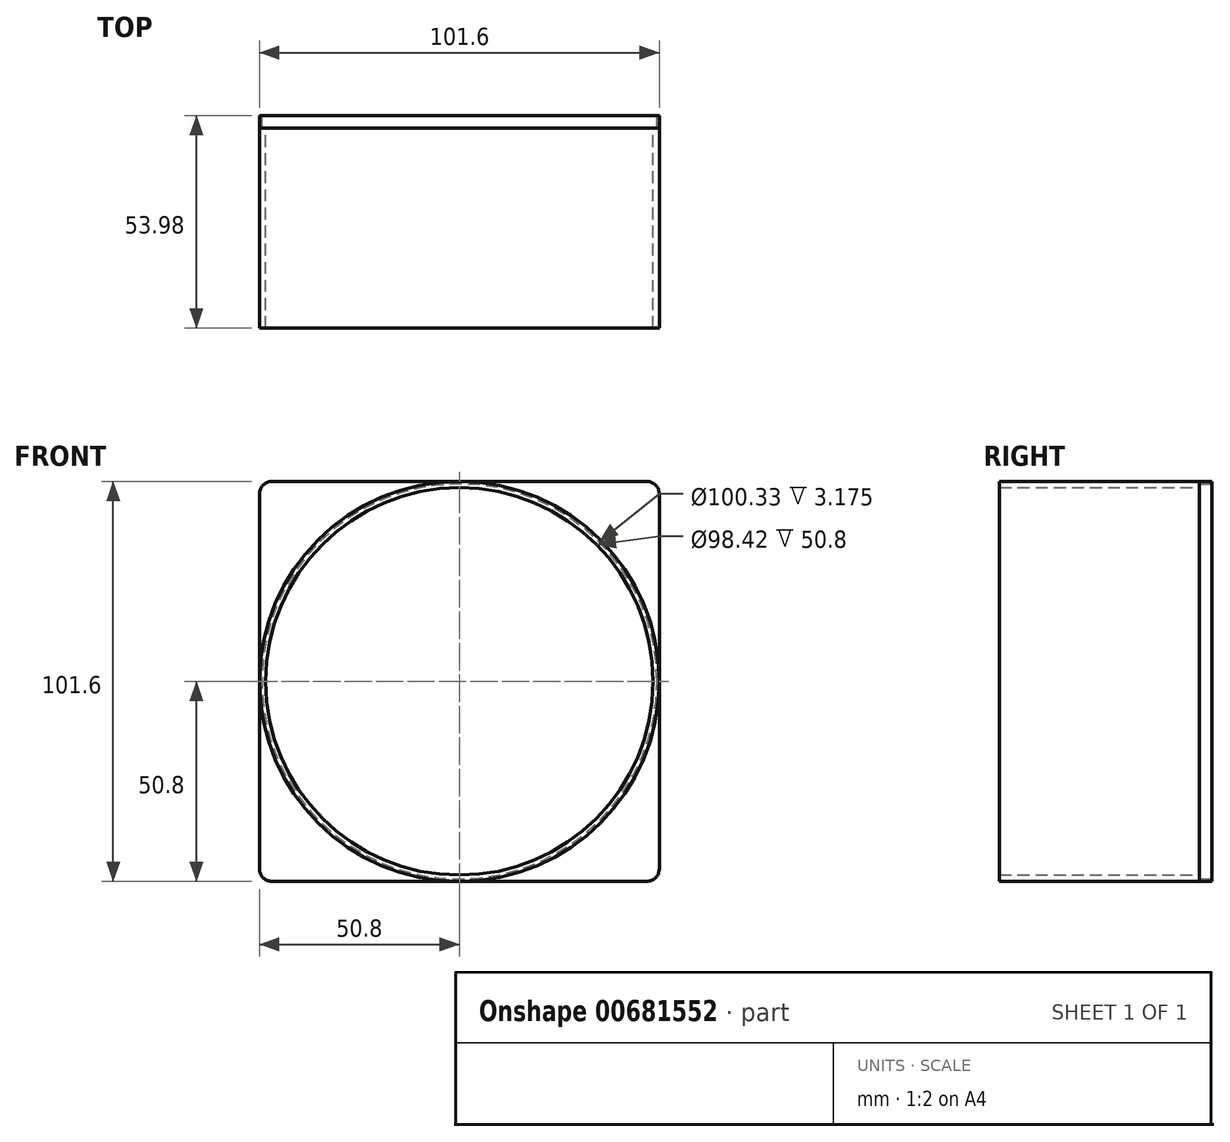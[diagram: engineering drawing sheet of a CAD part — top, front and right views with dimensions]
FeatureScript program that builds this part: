
annotation { "Feature Type Name" : "Feature", "Feature Type Description" : "" }
export const myFeature = defineFeature(function(context is Context, id is Id, definition is map)
    precondition{}
    {
        {
            var Q0;
            Q0=qCreatedBy(makeId("Front.planeOp"),FACE);
            var sketch = newSketch(context, id + "F0", { "sketchPlane" : qUnion([Q0])});
            skLineSegment(sketch, "E0.bottom", {"start": v(47.62, 50.8) * mm, "end": v(-47.62, 50.8) * mm});
            skLineSegment(sketch, "E0.top", {"start": v(47.62, -50.8) * mm, "end": v(-47.62, -50.8) * mm});
            skLineSegment(sketch, "E0.left", {"start": v(50.8, 47.62) * mm, "end": v(50.8, -47.62) * mm});
            skLineSegment(sketch, "E0.right", {"start": v(-50.8, 47.62) * mm, "end": v(-50.8, -47.62) * mm});
            skPoint(sketch, "E0.middle", {"position": v(0, 0) * mm});
            skPoint(sketch, "E1.visualSharp", {"position": v(-50.8, 50.8) * mm});
            skArc(sketch, "E1.filletArc", {"start": v(-47.62, 50.8) * mm, "mid": v(-49.87, 49.87) * mm, "end": v(-50.8, 47.62) * mm});
            skPoint(sketch, "E2.visualSharp", {"position": v(50.8, 50.8) * mm});
            skArc(sketch, "E2.filletArc", {"start": v(50.8, 47.62) * mm, "mid": v(49.87, 49.87) * mm, "end": v(47.62, 50.8) * mm});
            skPoint(sketch, "E3.visualSharp", {"position": v(-50.8, -50.8) * mm});
            skArc(sketch, "E3.filletArc", {"start": v(-50.8, -47.62) * mm, "mid": v(-49.87, -49.87) * mm, "end": v(-47.62, -50.8) * mm});
            skPoint(sketch, "E4.visualSharp", {"position": v(50.8, -50.8) * mm});
            skArc(sketch, "E4.filletArc", {"start": v(47.62, -50.8) * mm, "mid": v(49.87, -49.87) * mm, "end": v(50.8, -47.62) * mm});
            skCircle(sketch, "E5", {"center": v(0, 0) * mm, "radius": 50.17 * mm});
            skSolve(sketch);
        }
        {
            var Q0;
            Q0 = qSketchRegion(id + "F0", true);
            extrude(context, id + "F1", {"entities" : qUnion([Q0]), "depth" : 3.17 * mm, "offsetDistance" : 25.4 * mm});
        }
        {
            var Q0;
            Q0=makeQuery(id+"F1.opExtrude","CAP_FACE",FACE,{"disambiguationData":[OSD([sQuery(id+"F0.wireOp",EDGE,"E0.bottom"),sQuery(id+"F0.wireOp",EDGE,"E0.top"),sQuery(id+"F0.wireOp",EDGE,"E0.left"),sQuery(id+"F0.wireOp",EDGE,"E0.right"),sQuery(id+"F0.wireOp",EDGE,"E1.filletArc"),sQuery(id+"F0.wireOp",EDGE,"E2.filletArc"),sQuery(id+"F0.wireOp",EDGE,"E3.filletArc"),sQuery(id+"F0.wireOp",EDGE,"E4.filletArc"),sQuery(id+"F0.wireOp",EDGE,"E5")])],"isStart":false});
            var sketch = newSketch(context, id + "F2", { "sketchPlane" : qUnion([Q0])});
            skCircle(sketch, "E6", {"center": v(0, 0) * mm, "radius": 50.8 * mm});
            skCircle(sketch, "E7.0", {"center": v(0, 0) * mm, "radius": 49.21 * mm});
            skSolve(sketch);
        }
        {
            var Q0;
            Q0 = qSketchRegion(id + "F2", true);
            extrude(context, id + "F3", {"entities" : qUnion([Q0]), "operationType" : NewBodyOperationType.ADD, "depth" : 50.8 * mm, "offsetDistance" : 25.4 * mm});
        }
    });
